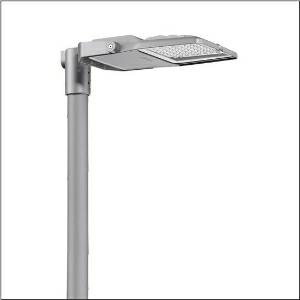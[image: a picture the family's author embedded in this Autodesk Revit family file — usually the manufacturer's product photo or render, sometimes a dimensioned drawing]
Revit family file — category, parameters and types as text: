
# Revit family: floodlight_fl_21_iq_mini___pl52_5xa7772d2d3a_9966
name_source: partatom
category: Lighting Fixtures
units: mm (PartAtom-declared; Revit-internal decimal feet)

## family parameters
Cut with Voids When Loaded = No
Host = Face
Light Source = No
Part Type = Normal
Room Calculation Point = No
Round Connector Dimension = Use Diameter
Shared = No

## types (1)
- --- (1 x LED, 17830 lm, 143 W, 3000K)
    Apparent Load = 143 VA
    CIE Flux Codes = 26 60 98 100 100
    Color Rendering = 70
    Color Temperature = 3000K
    Default Elevation = 1800 mm
    Description = Floodlight FL 21 iQ mini, floodlight, primary light control with lens, of PMMA, primary optical cover: protective disc, of toughened safety glass, transparent, light distribution: PL52, light emission: direct distribution, installation type: surface-mounted, LED, High Power LED, rated luminous flux: 17.830lm, luminous efficacy: 125lm/W, light colour: 730, colour temperature: 3000K, control gear: iQ Street-Remote/DALI, control: Auto-Match, Temp-Guard, Night-Set, Smart-Wire, Desk-Remote (wireless, voltage-free reading and setting of iQ features in the workshop via application-optimized NFC function/RFID function), optimised constant luminous flux control (CLO 2.0), Light-Fading, Lumen-Switch, with terminal, 6-pole, mains connection: 220..240V, AC, 50/60Hz, start of lifetime: 143W, end of service life: 152W, reduction: 61W, luminaire housing, of diecast aluminium, powder-coated, Siteco® metallic grey (DB 702S), corrosivity category C5 mid according to DIN EN ISO 12944, suitable for swimming pools, chlorine-resistant, sealing non-destructively replaceable, please order mast flange separately, mast bracket, of steel, galvanised, powder-coated, protection rating (complete): IP66, insulation class (complete): insulation class II (safety insulation), certification: CE, ENEC, VDE, protection symbol: D, impact resistance: IK08, permissible operating ambient temperature: -40..+40°C, permissible operating ambient temperature for outdoor applications: -40..+50°C, standard: DIN EN 12944, LABS conformity tested according to VDMA 24364:2018-05, packaging unit: 1 piece

Light Distribution: PL52
    Height = 70 mm
    Lamp = 1 x LED
    Lamp Light Flux = 17830 lm
    Lamp Power = 143 W
    Lamp count = 1
    Length = 485 mm
    Luminous efficacy = 125 lm/W
    Manufacturer = Siteco
    ModVariant = No
    Model = 5XA7772D2D3A
    Number of Poles = 1
    OnlyDefault = Yes
    Power Factor = 1
    Product Name = Floodlight FL 21 iQ mini | PL52
    Product group = floodlight | pylon annexe
    ProductGroupID = 6201
    Protection Class = Protection class II
    Protection Degree = IP 66
    RLX_Detail_Level = 1
    RLX_Emergency_Light_Flux = 0 lm
    RLX_Emergency_Type = 0
    RLX_Emergency_Type_DB = No
    RlxData = <blob elided: 101853 chars, md5=5ede8af9>
    Socket = socket
    Standby Power = 0 W
    System Light Flux = 17830 lm
    System Power = 143 W
    Type Comments = factory setting: luminous flux: 100 % | dim-lin: 254 | 730 mA
    Type Image = l_1007125.jpg
    URL = http://relux.com
    VarID = @adj_185169
    Voltage = 0 V
    Weight = 0.00 kg
    Width = 337 mm

## geometry (parser evidence)
native form markers: Blend x4, Sweep x10
no freeform markers — native parametric forms only
